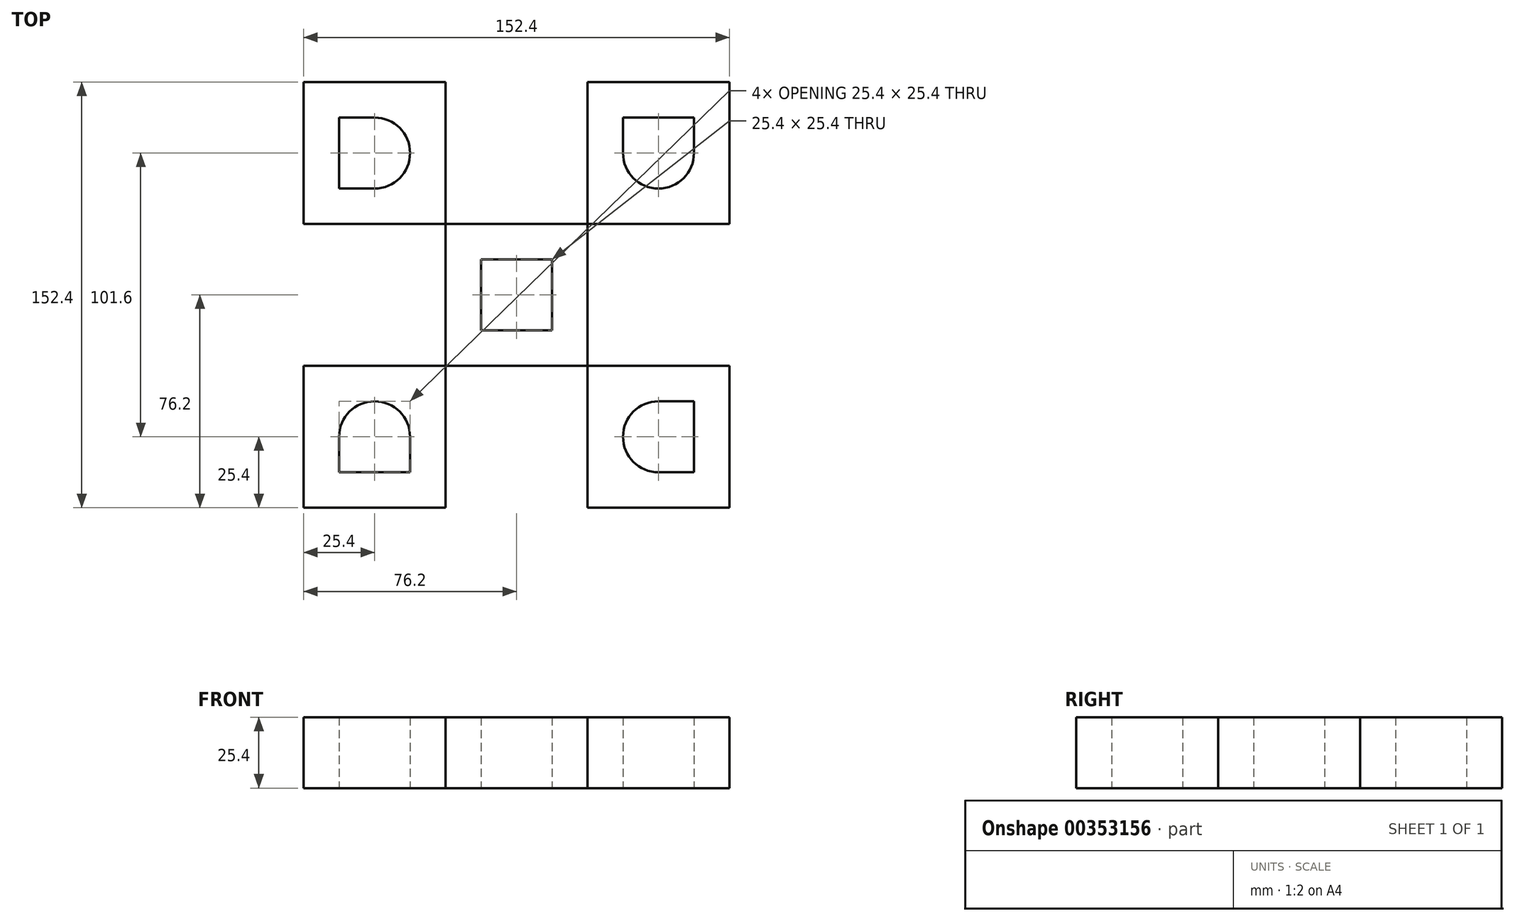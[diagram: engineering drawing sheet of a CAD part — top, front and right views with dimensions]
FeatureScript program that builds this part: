
annotation { "Feature Type Name" : "Feature", "Feature Type Description" : "" }
export const myFeature = defineFeature(function(context is Context, id is Id, definition is map)
    precondition{}
    {
        {
            var Q0;
            Q0=qCreatedBy(makeId("Top.planeOp"),FACE);
            var sketch = newSketch(context, id + "F0", { "sketchPlane" : qUnion([Q0])});
            skLineSegment(sketch, "E0.bottom", {"start": v(0, 0) * mm, "end": v(50.8, 0) * mm});
            skLineSegment(sketch, "E0.top", {"start": v(0, 50.8) * mm, "end": v(50.8, 50.8) * mm});
            skLineSegment(sketch, "E0.left", {"start": v(0, 0) * mm, "end": v(0, 50.8) * mm});
            skLineSegment(sketch, "E0.right", {"start": v(50.8, 0) * mm, "end": v(50.8, 50.8) * mm});
            skLineSegment(sketch, "E1.bottom", {"start": v(50.8, 50.8) * mm, "end": v(101.6, 50.8) * mm});
            skLineSegment(sketch, "E1.top", {"start": v(50.8, 101.6) * mm, "end": v(101.6, 101.6) * mm});
            skLineSegment(sketch, "E1.left", {"start": v(50.8, 50.8) * mm, "end": v(50.8, 101.6) * mm});
            skLineSegment(sketch, "E1.right", {"start": v(101.6, 50.8) * mm, "end": v(101.6, 101.6) * mm});
            skLineSegment(sketch, "E2.bottom", {"start": v(50.8, 0) * mm, "end": v(101.6, 0) * mm});
            skLineSegment(sketch, "E2.top", {"start": v(50.8, -50.8) * mm, "end": v(101.6, -50.8) * mm});
            skLineSegment(sketch, "E2.left", {"start": v(50.8, 0) * mm, "end": v(50.8, -50.8) * mm});
            skLineSegment(sketch, "E2.right", {"start": v(101.6, 0) * mm, "end": v(101.6, -50.8) * mm});
            skLineSegment(sketch, "E3.bottom", {"start": v(0, 50.8) * mm, "end": v(-50.8, 50.8) * mm});
            skLineSegment(sketch, "E3.top", {"start": v(0, 101.6) * mm, "end": v(-50.8, 101.6) * mm});
            skLineSegment(sketch, "E3.left", {"start": v(0, 50.8) * mm, "end": v(0, 101.6) * mm});
            skLineSegment(sketch, "E3.right", {"start": v(-50.8, 50.8) * mm, "end": v(-50.8, 101.6) * mm});
            skLineSegment(sketch, "E4.bottom", {"start": v(0, 0) * mm, "end": v(-50.8, 0) * mm});
            skLineSegment(sketch, "E4.top", {"start": v(0, -50.8) * mm, "end": v(-50.8, -50.8) * mm});
            skLineSegment(sketch, "E4.left", {"start": v(0, 0) * mm, "end": v(0, -50.8) * mm});
            skLineSegment(sketch, "E4.right", {"start": v(-50.8, 0) * mm, "end": v(-50.8, -50.8) * mm});
            skLineSegment(sketch, "E5.bottom", {"start": v(38.1, 12.7) * mm, "end": v(12.7, 12.7) * mm});
            skLineSegment(sketch, "E5.top", {"start": v(38.1, 38.1) * mm, "end": v(12.7, 38.1) * mm});
            skLineSegment(sketch, "E5.left", {"start": v(38.1, 12.7) * mm, "end": v(38.1, 38.1) * mm});
            skLineSegment(sketch, "E5.right", {"start": v(12.7, 12.7) * mm, "end": v(12.7, 38.1) * mm});
            skPoint(sketch, "E5.middle", {"position": v(25.4, 25.4) * mm});
            skPoint(sketch, "E5.middle.positionSnap0", {"position": v(50.8, 25.4) * mm});
            skPoint(sketch, "E5.middle.positionSnap1", {"position": v(25.4, 50.8) * mm});
            skPoint(sketch, "E5.centerSnap0", {"position": v(50.8, 25.4) * mm});
            skPoint(sketch, "E5.centerSnap1", {"position": v(25.4, 50.8) * mm});
            skLineSegment(sketch, "E6.bottom", {"start": v(88.9, 88.9) * mm, "end": v(63.5, 88.9) * mm});
            skLineSegment(sketch, "E6.left", {"start": v(88.9, 88.9) * mm, "end": v(88.9, 76.2) * mm});
            skLineSegment(sketch, "E6.right", {"start": v(63.5, 88.9) * mm, "end": v(63.5, 76.2) * mm});
            skPoint(sketch, "E6.middle", {"position": v(76.2, 76.2) * mm});
            skPoint(sketch, "E6.middle.positionSnap0", {"position": v(101.6, 76.2) * mm});
            skPoint(sketch, "E6.middle.positionSnap1", {"position": v(76.2, 101.6) * mm});
            skPoint(sketch, "E6.centerSnap0", {"position": v(101.6, 76.2) * mm});
            skPoint(sketch, "E6.centerSnap1", {"position": v(76.2, 101.6) * mm});
            skLineSegment(sketch, "E7.bottom", {"start": v(-25.4, 88.9) * mm, "end": v(-38.1, 88.9) * mm});
            skLineSegment(sketch, "E7.top", {"start": v(-25.4, 63.5) * mm, "end": v(-38.1, 63.5) * mm});
            skLineSegment(sketch, "E7.right", {"start": v(-38.1, 88.9) * mm, "end": v(-38.1, 63.5) * mm});
            skPoint(sketch, "E7.middle", {"position": v(-25.4, 76.2) * mm});
            skPoint(sketch, "E7.middle.positionSnap0", {"position": v(0, 76.2) * mm});
            skPoint(sketch, "E7.middle.positionSnap1", {"position": v(-25.4, 101.6) * mm});
            skPoint(sketch, "E7.centerSnap0", {"position": v(0, 76.2) * mm});
            skPoint(sketch, "E7.centerSnap1", {"position": v(-25.4, 101.6) * mm});
            skLineSegment(sketch, "E8.top", {"start": v(-12.7, -38.1) * mm, "end": v(-38.1, -38.1) * mm});
            skLineSegment(sketch, "E8.left", {"start": v(-12.7, -25.4) * mm, "end": v(-12.7, -38.1) * mm});
            skLineSegment(sketch, "E8.right", {"start": v(-38.1, -25.4) * mm, "end": v(-38.1, -38.1) * mm});
            skPoint(sketch, "E8.middle", {"position": v(-25.4, -25.4) * mm});
            skPoint(sketch, "E8.middle.positionSnap0", {"position": v(0, -25.4) * mm});
            skPoint(sketch, "E8.middle.positionSnap1", {"position": v(-25.4, 0) * mm});
            skPoint(sketch, "E8.centerSnap0", {"position": v(0, -25.4) * mm});
            skPoint(sketch, "E8.centerSnap1", {"position": v(-25.4, 0) * mm});
            skLineSegment(sketch, "E9.bottom", {"start": v(88.9, -12.7) * mm, "end": v(76.2, -12.7) * mm});
            skLineSegment(sketch, "E9.top", {"start": v(88.9, -38.1) * mm, "end": v(76.2, -38.1) * mm});
            skLineSegment(sketch, "E9.left", {"start": v(88.9, -12.7) * mm, "end": v(88.9, -38.1) * mm});
            skPoint(sketch, "E9.middle", {"position": v(76.2, -25.4) * mm});
            skPoint(sketch, "E9.middle.positionSnap0", {"position": v(101.6, -25.4) * mm});
            skPoint(sketch, "E9.middle.positionSnap1", {"position": v(76.2, 0) * mm});
            skPoint(sketch, "E9.centerSnap0", {"position": v(101.6, -25.4) * mm});
            skPoint(sketch, "E9.centerSnap1", {"position": v(76.2, 0) * mm});
            skArc(sketch, "E10", {"start": v(63.5, 76.2) * mm, "mid": v(76.2, 63.5) * mm, "end": v(88.9, 76.2) * mm});
            skArc(sketch, "E11", {"start": v(-25.4, 63.5) * mm, "mid": v(-12.7, 76.2) * mm, "end": v(-25.4, 88.9) * mm});
            skArc(sketch, "E12", {"start": v(-12.7, -25.4) * mm, "mid": v(-25.4, -12.7) * mm, "end": v(-38.1, -25.4) * mm});
            skArc(sketch, "E13", {"start": v(76.2, -12.7) * mm, "mid": v(63.5, -25.4) * mm, "end": v(76.2, -38.1) * mm});
            skPoint(sketch, "E14.orphan", {"position": v(63.5, 63.5) * mm});
            skPoint(sketch, "E15.orphan", {"position": v(88.9, 63.5) * mm});
            skPoint(sketch, "E16.orphan", {"position": v(63.5, -12.7) * mm});
            skPoint(sketch, "E17.orphan", {"position": v(63.5, -38.1) * mm});
            skPoint(sketch, "E18.orphan", {"position": v(-38.1, -12.7) * mm});
            skPoint(sketch, "E19.orphan", {"position": v(-12.7, -12.7) * mm});
            skPoint(sketch, "E20.orphan", {"position": v(-12.7, 88.9) * mm});
            skPoint(sketch, "E21.orphan", {"position": v(-12.7, 63.5) * mm});
            skSolve(sketch);
        }
        {
            var Q0;
            Q0 = qSketchRegion(id + "F0", true);
            extrude(context, id + "F1", {"entities" : qUnion([Q0]), "depth" : 25.4 * mm});
        }
    });
